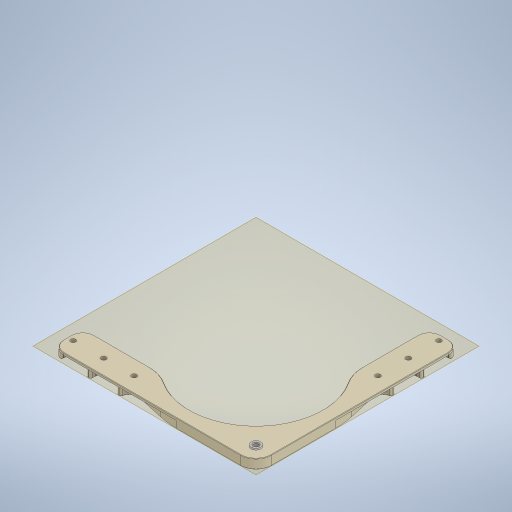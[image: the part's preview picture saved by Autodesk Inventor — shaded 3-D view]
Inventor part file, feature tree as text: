
AUTODESK INVENTOR PART (.ipt)
format: ipt  version: 2023.3 (Build 273359000, 359)  size: 1,758,720 bytes
history: native  units: in
note: dims shown in document units (in); Inventor stores cm internally (conversion verified against a paired STEP export)
features: other x16, chamfer x3, plane x1
ambient origin geometry x8: Origin, YZ Plane, XZ Plane, XY Plane, X Axis, Y Axis, Z Axis, Center Point
bodies: Solid1 (feature_tree), Solid2 (feature_tree), Solid3 (feature_tree), Solid4 (feature_tree), Solid5 (feature_tree), Solid6 (feature_tree), Solid7 (feature_tree), Solid8 (feature_tree), Solid9 (feature_tree), Solid10 (feature_tree), Solid11 (feature_tree), Solid12 (feature_tree), Solid13 (feature_tree), Solid14 (feature_tree), Solid15 (feature_tree), Solid16 (feature_tree), Solid17 (feature_tree), Solid18 (feature_tree), Solid19 (feature_tree)
feature tree (20):
  plane  "Work Plane1"
  other  "Boss-Extrude4[1]"
  other  "Boss-Extrude4[2]"
  other  "Boss-Extrude4[3]"
  other  "Boss-Extrude6[1]"
  other  "Boss-Extrude6[2]"
  other  "Boss-Extrude6[3]"
  other  "Boss-Extrude6[4]"
  other  "Boss-Extrude6[5]"
  other  "Boss-Extrude6[6]"
  other  "Boss-Extrude6[7]"
  other  "Boss-Extrude6[8]"
  other  "Boss-Extrude9[1]"
  other  "Boss-Extrude17[1]"
  other  "Boss-Extrude17[2]"
  other  "Boss-Extrude17[3]"
  chamfer  "Chamfer4"  [1 undecoded]
  other  "Move Face1"
  chamfer  "Chamfer1"  [1 undecoded]
  chamfer  "Chamfer2"  [1 undecoded]
note: 3 required parameter values undecoded (feature->parameter linkage not recoverable at this tier; creation-order binding heuristic only, values carry confidence <= 0.55)
